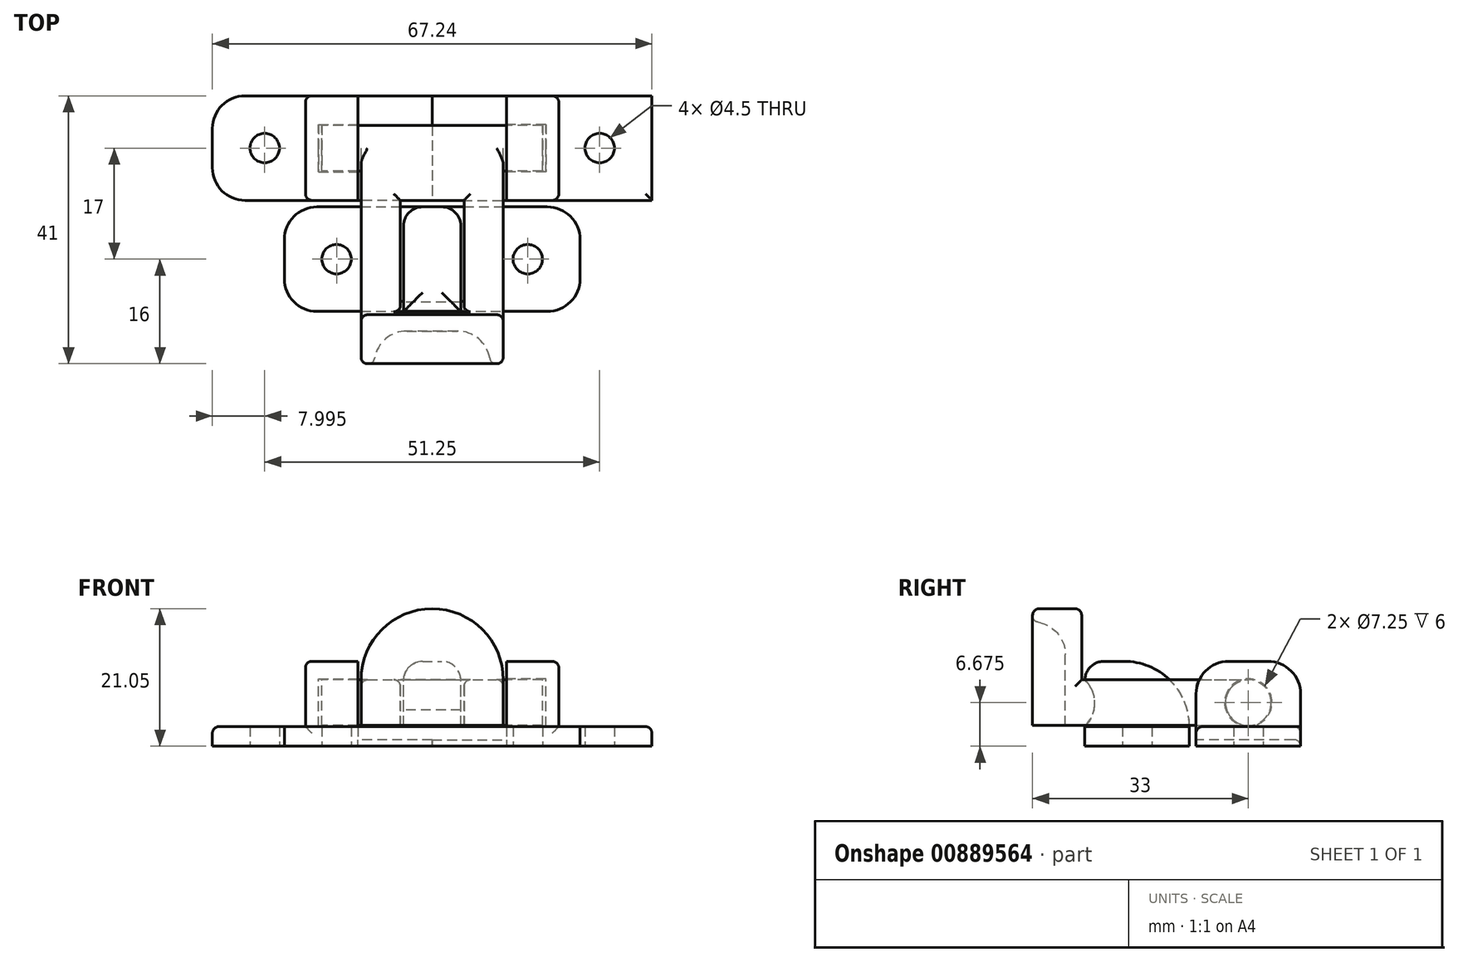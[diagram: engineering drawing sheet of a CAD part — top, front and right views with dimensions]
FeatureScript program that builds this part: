
annotation { "Feature Type Name" : "Feature", "Feature Type Description" : "" }
export const myFeature = defineFeature(function(context is Context, id is Id, definition is map)
    precondition{}
    {
        {
            var Q0;
            Q0=qCreatedBy(makeId("Top.planeOp"),FACE);
            var sketch = newSketch(context, id + "F0", { "sketchPlane" : qUnion([Q0])});
            skCircle(sketch, "E0", {"center": v(-25.62, 8.5) * mm, "radius": 2.25 * mm});
            skCircle(sketch, "E1", {"center": v(25.62, 8.5) * mm, "radius": 2.25 * mm});
            skCircle(sketch, "E2", {"center": v(-14.62, -8.5) * mm, "radius": 2.25 * mm});
            skCircle(sketch, "E3", {"center": v(14.63, -8.5) * mm, "radius": 2.25 * mm});
            skLineSegment(sketch, "E4", {"start": v(-25.62, 8.5) * mm, "end": v(25.62, 8.5) * mm, "construction": true});
            skLineSegment(sketch, "E5", {"start": v(-14.62, -8.5) * mm, "end": v(14.63, -8.5) * mm, "construction": true});
            skPoint(sketch, "E6", {"position": v(0, 8.5) * mm});
            skPoint(sketch, "E7", {"position": v(0, -8.5) * mm});
            skLineSegment(sketch, "E8.bottom", {"start": v(-33.62, 16.5) * mm, "end": v(33.62, 16.5) * mm});
            skLineSegment(sketch, "E8.top", {"start": v(-33.62, 0.5) * mm, "end": v(33.62, 0.5) * mm});
            skLineSegment(sketch, "E8.left", {"start": v(-33.63, 16.5) * mm, "end": v(-33.63, 0.5) * mm});
            skLineSegment(sketch, "E8.right", {"start": v(33.63, 16.5) * mm, "end": v(33.63, 0.5) * mm});
            skLineSegment(sketch, "E9.bottom", {"start": v(-22.62, -0.5) * mm, "end": v(22.62, -0.5) * mm});
            skLineSegment(sketch, "E9.top", {"start": v(-22.62, -16.5) * mm, "end": v(22.63, -16.5) * mm});
            skLineSegment(sketch, "E9.left", {"start": v(-22.63, -0.5) * mm, "end": v(-22.63, -16.5) * mm});
            skLineSegment(sketch, "E9.right", {"start": v(22.63, -0.5) * mm, "end": v(22.63, -16.5) * mm});
            skLineSegment(sketch, "E10", {"start": v(0, -0.5) * mm, "end": v(0, 0) * mm, "construction": true});
            skLineSegment(sketch, "E11", {"start": v(0, 0) * mm, "end": v(0, 0.5) * mm});
            skLineSegment(sketch, "E12", {"start": v(0, 0.5) * mm, "end": v(0, 0) * mm, "construction": true});
            skLineSegment(sketch, "E13", {"start": v(-11.38, 16.5) * mm, "end": v(-11.38, 0.5) * mm});
            skLineSegment(sketch, "E14", {"start": v(11.38, 16.5) * mm, "end": v(11.38, 0.5) * mm});
            skSolve(sketch);
        }
        {
            var Q0;
            Q0=makeQuery(id+"F0.imprint","IMPRINT",FACE,{"disambiguationData":[TD([[makeQuery(id+"F0.imprint","IMPRINT",EDGE,{"derivedFrom":sQuery(id+"F0.wireOp",EDGE,"E0")}),-1.0]])]});
            var Q1;
            Q1=makeQuery(id+"F0.imprint","IMPRINT",FACE,{"disambiguationData":[TD([[makeQuery(id+"F0.imprint","IMPRINT",EDGE,{"derivedFrom":sQuery(id+"F0.wireOp",EDGE,"E2")}),-1.0]])]});
            extrude(context, id + "F1", {"entities" : qUnion([Q0, Q1]), "depth" : 3 * mm, "offsetDistance" : 25 * mm});
        }
        {
            var Q0;
            Q0=makeQuery(id+"F1.opExtrude","CAP_FACE",FACE,{"disambiguationData":[OSD([sQuery(id+"F0.wireOp",EDGE,"E2"),sQuery(id+"F0.wireOp",EDGE,"E3"),sQuery(id+"F0.wireOp",EDGE,"E9.bottom"),sQuery(id+"F0.wireOp",EDGE,"E9.top"),sQuery(id+"F0.wireOp",EDGE,"E9.left"),sQuery(id+"F0.wireOp",EDGE,"E9.right")])],"isStart":false});
            var sketch = newSketch(context, id + "F2", { "sketchPlane" : qUnion([Q0])});
            skLineSegment(sketch, "E15.bottom", {"start": v(-4.38, -0.5) * mm, "end": v(4.38, -0.5) * mm});
            skLineSegment(sketch, "E15.top", {"start": v(-4.37, -16.5) * mm, "end": v(4.38, -16.5) * mm});
            skLineSegment(sketch, "E15.left", {"start": v(-4.38, -0.5) * mm, "end": v(-4.37, -16.5) * mm});
            skLineSegment(sketch, "E15.right", {"start": v(4.38, -0.5) * mm, "end": v(4.38, -16.5) * mm});
            skLineSegment(sketch, "E16", {"start": v(-4.38, -8.5) * mm, "end": v(-12.38, -8.5) * mm, "construction": true});
            skLineSegment(sketch, "E17", {"start": v(4.38, -8.5) * mm, "end": v(12.38, -8.5) * mm, "construction": true});
            skSolve(sketch);
        }
        {
            var Q0;
            Q0=makeQuery(id+"F2.imprint","IMPRINT",FACE,{"disambiguationData":[TD([[makeQuery(id+"F2.imprint","IMPRINT",EDGE,{"derivedFrom":sQuery(id+"F2.wireOp",EDGE,"E15.bottom")}),-1.0]])]});
            extrude(context, id + "F3", {"entities" : qUnion([Q0]), "operationType" : NewBodyOperationType.ADD, "depth" : 10 * mm, "offsetDistance" : 25 * mm});
        }
        {
            var Q0;
            Q0=makeQuery(id+"F3.opExtrude","SWEPT_FACE",FACE,{"disambiguationData":[OSD([sQuery(id+"F2.wireOp",EDGE,"E15.right")])]});
            var sketch = newSketch(context, id + "F4", { "sketchPlane" : qUnion([Q0])});
            skArc(sketch, "E18", {"start": v(-16.5, 3) * mm, "mid": v(-15, 6.55) * mm, "end": v(-16.5, 10.1) * mm});
            skSolve(sketch);
        }
        {
            var Q0;
            {var subQ0=sQuery(id+"F4.wireOp",EDGE,"E18");Q0=makeQuery(id+"F4.imprint","IMPRINT",FACE,{"disambiguationData":[TD([[makeQuery(id+"F4.imprint","IMPRINT",EDGE,{"derivedFrom":subQ0}),1.0]])]});}
            extrude(context, id + "F5", {"entities" : qUnion([Q0]), "operationType" : NewBodyOperationType.REMOVE, "oppositeDirection" : true, "depth" : 25 * mm, "offsetDistance" : 25 * mm});
        }
        {
            var Q0;
            Q0=makeQuery(id+"F1.opExtrude","CAP_FACE",FACE,{"disambiguationData":[OSD([sQuery(id+"F0.wireOp",EDGE,"E0"),sQuery(id+"F0.wireOp",EDGE,"E8.bottom"),sQuery(id+"F0.wireOp",EDGE,"E8.top"),sQuery(id+"F0.wireOp",EDGE,"E8.left"),sQuery(id+"F0.wireOp",EDGE,"E13")])],"isStart":false});
            var sketch = newSketch(context, id + "F6", { "sketchPlane" : qUnion([Q0])});
            skLineSegment(sketch, "E19", {"start": v(-19.37, 16.5) * mm, "end": v(-19.37, 0.5) * mm});
            skSolve(sketch);
        }
        {
            var Q0;
            {var subQ0=sQuery(id+"F6.wireOp",EDGE,"E19");Q0=makeQuery(id+"F6.imprint","IMPRINT",FACE,{"disambiguationData":[TD([[makeQuery(id+"F6.imprint","IMPRINT",EDGE,{"derivedFrom":subQ0}),1.0]])]});}
            extrude(context, id + "F7", {"entities" : qUnion([Q0]), "operationType" : NewBodyOperationType.ADD, "depth" : 10 * mm, "offsetDistance" : 25 * mm});
        }
        {
            var Q0;
            {var subQ0=sQuery(id+"F0.wireOp",EDGE,"E13");Q0=makeQuery(id+"F7.boolean.opBoolean","MERGE",FACE,{"derivedFrom":[makeQuery(id+"F1.opExtrude","SWEPT_FACE",FACE,{"disambiguationData":[OSD([subQ0])]}),makeQuery(id+"F7.opExtrude","SWEPT_FACE",FACE,{"disambiguationData":[OSD([subQ0])]})]});}
            var sketch = newSketch(context, id + "F8", { "sketchPlane" : qUnion([Q0])});
            skCircle(sketch, "E20", {"center": v(8.5, 6.68) * mm, "radius": 3.62 * mm});
            skPoint(sketch, "E21", {"position": v(8.5, 13) * mm});
            skSolve(sketch);
        }
        {
            var Q0;
            Q0=makeQuery(id+"F8.imprint","IMPRINT",FACE,{"disambiguationData":[TD([[makeQuery(id+"F8.imprint","IMPRINT",EDGE,{"derivedFrom":sQuery(id+"F8.wireOp",EDGE,"E20")}),1.0]])]});
            extrude(context, id + "F9", {"entities" : qUnion([Q0]), "operationType" : NewBodyOperationType.REMOVE, "oppositeDirection" : true, "depth" : 6 * mm, "offsetDistance" : 25 * mm});
        }
        {
            var Q0;
            Q0=makeQuery(id+"F9.boolean.opBoolean","COPY",FACE,{"derivedFrom":makeQuery(id+"F9.opExtrude","CAP_FACE",FACE,{"disambiguationData":[OSD([sQuery(id+"F8.wireOp",EDGE,"E20")])],"isStart":false})});
            cPlane(context, id + "F10", {"entities" : qUnion([Q0]), "cplaneType" : CPlaneType.OFFSET, "offset" : .5 * mm, "width" : 150 * mm, "height" : 150 * mm});
        }
        {
            var Q0;
            {var subQ0=sQuery(id+"F0.wireOp",EDGE,"E13");Q0=makeQuery(id+"F7.boolean.opBoolean","MERGE",FACE,{"derivedFrom":[makeQuery(id+"F1.opExtrude","SWEPT_FACE",FACE,{"disambiguationData":[OSD([subQ0])]}),makeQuery(id+"F7.opExtrude","SWEPT_FACE",FACE,{"disambiguationData":[OSD([subQ0])]})]});}
            var sketch = newSketch(context, id + "F11", { "sketchPlane" : qUnion([Q0])});
            skLineSegment(sketch, "E22", {"start": v(16.5, 1) * mm, "end": v(0.5, 1) * mm});
            skSolve(sketch);
        }
        {
            var Q0;
            {var subQ0=sQuery(id+"F11.wireOp",EDGE,"E22");Q0=makeQuery(id+"F11.imprint","IMPRINT",FACE,{"disambiguationData":[TD([[makeQuery(id+"F11.imprint","IMPRINT",EDGE,{"derivedFrom":subQ0}),1.0]])]});}
            var Q1;
            Q1=qCreatedBy(makeId("Right.planeOp"),FACE);
            extrude(context, id + "F12", {"entities" : qUnion([Q0]), "operationType" : NewBodyOperationType.ADD, "endBound" : BoundingType.UP_TO_SURFACE, "depth" : 25 * mm, "endBoundEntityFace" : qUnion([Q1]), "offsetDistance" : 25 * mm});
        }
        {
            var Q0;
            Q0=makeQuery(id+"F1.opExtrude","SWEPT_BODY",BODY,{"disambiguationData":[OSD([sQuery(id+"F0.wireOp",EDGE,"E0"),sQuery(id+"F0.wireOp",EDGE,"E8.bottom"),sQuery(id+"F0.wireOp",EDGE,"E8.top"),sQuery(id+"F0.wireOp",EDGE,"E8.left"),sQuery(id+"F0.wireOp",EDGE,"E13")])]});
            var Q1;
            Q1=qCreatedBy(makeId("Right.planeOp"),FACE);
            mirror(context, id + "F13", {"operationType" : NewBodyOperationType.ADD, "entities" : qUnion([Q0]), "mirrorPlane" : qUnion([Q1])});
        }
        {
            var Q0;
            Q0=qCreatedBy(id+"F10.planeOp",FACE);
            var sketch = newSketch(context, id + "F14", { "sketchPlane" : qUnion([Q0])});
            skCircle(sketch, "E23", {"center": v(8.5, 6.68) * mm, "radius": 3.5 * mm});
            skSolve(sketch);
        }
        {
            var Q0;
            Q0=makeQuery(id+"F14.imprint","IMPRINT",FACE,{"disambiguationData":[TD([[makeQuery(id+"F14.imprint","IMPRINT",EDGE,{"derivedFrom":sQuery(id+"F14.wireOp",EDGE,"E23")}),1.0]])]});
            var Q1;
            Q1=qCreatedBy(makeId("Right.planeOp"),FACE);
            extrude(context, id + "F15", {"entities" : qUnion([Q0]), "endBound" : BoundingType.UP_TO_SURFACE, "depth" : 30 * mm, "endBoundEntityFace" : qUnion([Q1]), "offsetDistance" : 25 * mm});
        }
        {
            var Q0;
            Q0=makeQuery(id+"F15.opExtrude","CAP_FACE",FACE,{"disambiguationData":[OSD([sQuery(id+"F14.wireOp",EDGE,"E23")])],"isStart":false});
            var sketch = newSketch(context, id + "F16", { "sketchPlane" : qUnion([Q0])});
            skLineSegment(sketch, "E24", {"start": v(8.5, 10.18) * mm, "end": v(0.5, 10.18) * mm});
            skLineSegment(sketch, "E25", {"start": v(8.5, 3.18) * mm, "end": v(0.5, 3.17) * mm});
            skLineSegment(sketch, "E26", {"start": v(0.5, 10.18) * mm, "end": v(0.5, 3.17) * mm});
            skArc(sketch, "E27", {"start": v(8.5, 3.18) * mm, "mid": v(12, 6.68) * mm, "end": v(8.5, 10.18) * mm});
            skSolve(sketch);
        }
        {
            var Q0;
            {var subQ0=sQuery(id+"F16.wireOp",EDGE,"E24");Q0=makeQuery(id+"F16.imprint","IMPRINT",FACE,{"disambiguationData":[TD([[makeQuery(id+"F16.imprint","IMPRINT",EDGE,{"derivedFrom":subQ0}),1.0]])]});}
            var Q1;
            {var subQ0=sQuery(id+"F0.wireOp",EDGE,"E13");Q1=makeQuery(id+"F7.boolean.opBoolean","MERGE",FACE,{"derivedFrom":[makeQuery(id+"F1.opExtrude","SWEPT_FACE",FACE,{"disambiguationData":[OSD([subQ0])]}),makeQuery(id+"F7.opExtrude","SWEPT_FACE",FACE,{"disambiguationData":[OSD([subQ0])]})]});}
            extrude(context, id + "F17", {"entities" : qUnion([Q0]), "operationType" : NewBodyOperationType.ADD, "endBound" : BoundingType.UP_TO_SURFACE, "oppositeDirection" : true, "depth" : 25 * mm, "endBoundEntityFace" : qUnion([Q1]), "hasOffset" : true, "offsetDistance" : .5 * mm});
        }
        {
            var Q0;
            Q0=makeQuery(id+"F17.opExtrude","SWEPT_FACE",FACE,{"disambiguationData":[OSD([sQuery(id+"F16.wireOp",EDGE,"E26")])]});
            var sketch = newSketch(context, id + "F18", { "sketchPlane" : qUnion([Q0])});
            skLineSegment(sketch, "E28", {"start": v(-4.87, 10.18) * mm, "end": v(-4.87, 3.17) * mm});
            skSolve(sketch);
        }
        {
            var Q0;
            {var subQ0=sQuery(id+"F18.wireOp",EDGE,"E28");Q0=makeQuery(id+"F18.imprint","IMPRINT",FACE,{"disambiguationData":[TD([[makeQuery(id+"F18.imprint","IMPRINT",EDGE,{"derivedFrom":subQ0}),-1.0]])]});}
            extrude(context, id + "F19", {"entities" : qUnion([Q0]), "operationType" : NewBodyOperationType.ADD, "depth" : 25 * mm, "offsetDistance" : 25 * mm});
        }
        {
            var Q0;
            Q0=makeQuery(id+"F19.opExtrude","SWEPT_FACE",FACE,{"disambiguationData":[OSD([sQuery(id+"F18.wireOp",EDGE,"E28")])]});
            var sketch = newSketch(context, id + "F20", { "sketchPlane" : qUnion([Q0])});
            skArc(sketch, "E29", {"start": v(-16.44, 3.17) * mm, "mid": v(-14.98, 6.7) * mm, "end": v(-16.55, 10.18) * mm});
            skSolve(sketch);
        }
        {
            var Q0;
            {var subQ0=sQuery(id+"F20.wireOp",EDGE,"E29");Q0=makeQuery(id+"F20.imprint","IMPRINT",FACE,{"disambiguationData":[TD([[makeQuery(id+"F20.imprint","IMPRINT",EDGE,{"derivedFrom":subQ0}),1.0]])]});}
            var Q1;
            {var subQ0=sQuery(id+"F14.wireOp",EDGE,"E23");Q1=makeQuery(id+"F17.boolean.opBoolean","MERGE",FACE,{"derivedFrom":[makeQuery(id+"F15.opExtrude","CAP_FACE",FACE,{"disambiguationData":[OSD([subQ0])],"isStart":false}),makeQuery(id+"F17.opExtrude","CAP_FACE",FACE,{"disambiguationData":[OSD([subQ0,sQuery(id+"F16.wireOp",EDGE,"E24"),sQuery(id+"F16.wireOp",EDGE,"E25"),sQuery(id+"F16.wireOp",EDGE,"E26")])],"isStart":true})]});}
            extrude(context, id + "F21", {"entities" : qUnion([Q0]), "endBound" : BoundingType.UP_TO_SURFACE, "depth" : 25 * mm, "endBoundEntityFace" : qUnion([Q1]), "offsetDistance" : 25 * mm});
        }
        {
            var Q0;
            Q0=makeQuery(id+"F15.opExtrude","SWEPT_BODY",BODY,{"disambiguationData":[OSD([sQuery(id+"F14.wireOp",EDGE,"E23")])]});
            var Q1;
            Q1=makeQuery(id+"F21.opExtrude","SWEPT_BODY",BODY,{"disambiguationData":[OSD([sQuery(id+"F16.wireOp",EDGE,"E24"),sQuery(id+"F16.wireOp",EDGE,"E25"),sQuery(id+"F16.wireOp",EDGE,"E26"),sQuery(id+"F18.wireOp",EDGE,"E28"),sQuery(id+"F20.wireOp",EDGE,"E29")])]});
            var Q2;
            Q2=qCreatedBy(makeId("Right.planeOp"),FACE);
            mirror(context, id + "F22", {"operationType" : NewBodyOperationType.ADD, "entities" : qUnion([Q0, Q1]), "mirrorPlane" : qUnion([Q2])});
        }
        {
            var Q0;
            {var subQ0=sQuery(id+"F18.wireOp",EDGE,"E28");var subQ1=makeQuery(id+"F21.opExtrude","SWEPT_FACE",FACE,{"disambiguationData":[OSD([subQ0])]});var subQ2=makeQuery(id+"F19.opExtrude","CAP_FACE",FACE,{"disambiguationData":[OSD([sQuery(id+"F16.wireOp",EDGE,"E24"),sQuery(id+"F16.wireOp",EDGE,"E25"),sQuery(id+"F16.wireOp",EDGE,"E26"),subQ0])],"isStart":false});Q0=makeQuery(id+"F22.boolean.opBoolean","MERGE",FACE,{"derivedFrom":[subQ2,subQ1,makeQuery(id+"F22.opPattern","COPY",FACE,{"derivedFrom":subQ2,"instanceName":"1"}),makeQuery(id+"F22.opPattern","COPY",FACE,{"derivedFrom":subQ1,"instanceName":"1"})]});}
            var sketch = newSketch(context, id + "F23", { "sketchPlane" : qUnion([Q0])});
            skArc(sketch, "E30", {"start": v(10.87, 10.18) * mm, "mid": v(0, 21.05) * mm, "end": v(-10.87, 10.18) * mm});
            skSolve(sketch);
        }
        {
            var Q0;
            Q0=qSketchRegion(id+"F23",true);
            var Q1;
            Q1=makeQuery(id+"F23.imprint","IMPRINT",FACE,{"disambiguationData":[TD([[makeQuery(id+"F23.imprint","IMPRINT",EDGE,{"derivedFrom":sQuery(id+"F23.wireOp",EDGE,"E30")}),1.0]])]});
            extrude(context, id + "F24", {"entities" : qUnion([Q0, Q1]), "operationType" : NewBodyOperationType.ADD, "depth" : -7.5 * mm, "offsetDistance" : 25 * mm});
        }
        {
            var Q0;
            {var subQ0=sQuery(id+"F18.wireOp",EDGE,"E28");var subQ1=sQuery(id+"F16.wireOp",EDGE,"E26");var subQ2=sQuery(id+"F16.wireOp",EDGE,"E24");var subQ3=makeQuery(id+"F21.opExtrude","SWEPT_FACE",FACE,{"disambiguationData":[OSD([subQ0])]});var subQ4=makeQuery(id+"F19.opExtrude","CAP_FACE",FACE,{"disambiguationData":[OSD([subQ2,sQuery(id+"F16.wireOp",EDGE,"E25"),subQ1,subQ0])],"isStart":false});Q0=makeQuery(id+"F24.boolean.opBoolean","MERGE",FACE,{"derivedFrom":[makeQuery(id+"F22.boolean.opBoolean","MERGE",FACE,{"derivedFrom":[subQ4,subQ3,makeQuery(id+"F22.opPattern","COPY",FACE,{"derivedFrom":subQ4,"instanceName":"1"}),makeQuery(id+"F22.opPattern","COPY",FACE,{"derivedFrom":subQ3,"instanceName":"1"})]}),makeQuery(id+"F24.opExtrude","CAP_FACE",FACE,{"disambiguationData":[OSD([subQ2,subQ1,subQ0,sQuery(id+"F23.wireOp",EDGE,"E30")])],"isStart":true})]});}
            var sketch = newSketch(context, id + "F25", { "sketchPlane" : qUnion([Q0])});
            skLineSegment(sketch, "E31.0", {"start": v(8.87, 3.17) * mm, "end": v(8.87, 10.18) * mm});
            skArc(sketch, "E31.1", {"start": v(8.87, 10.18) * mm, "mid": v(0, 19.05) * mm, "end": v(-8.87, 10.18) * mm});
            skLineSegment(sketch, "E31.2", {"start": v(-8.87, 3.17) * mm, "end": v(-8.87, 10.18) * mm});
            skSolve(sketch);
        }
        {
            var Q0;
            {var subQ0=sQuery(id+"F25.wireOp",EDGE,"E31.0");Q0=makeQuery(id+"F25.imprint","IMPRINT",FACE,{"disambiguationData":[TD([[makeQuery(id+"F25.imprint","IMPRINT",EDGE,{"derivedFrom":subQ0}),1.0]])]});}
            extrude(context, id + "F26", {"entities" : qUnion([Q0]), "operationType" : NewBodyOperationType.REMOVE, "oppositeDirection" : true, "depth" : 5 * mm, "offsetDistance" : 25 * mm});
        }
        {
            var Q0;
            Q0=makeQuery(id+"F7.opExtrude","CAP_EDGE",EDGE,{"disambiguationData":[OSD([sQuery(id+"F0.wireOp",EDGE,"E8.bottom")])],"isStart":false});
            var Q1;
            Q1=makeQuery(id+"F7.opExtrude","CAP_EDGE",EDGE,{"disambiguationData":[OSD([sQuery(id+"F0.wireOp",EDGE,"E8.top")])],"isStart":false});
            var Q2;
            Q2=makeQuery(id+"F13.opPattern","COPY",EDGE,{"derivedFrom":makeQuery(id+"F7.opExtrude","CAP_EDGE",EDGE,{"disambiguationData":[OSD([sQuery(id+"F0.wireOp",EDGE,"E8.bottom")])],"isStart":false}),"instanceName":"1"});
            var Q3;
            Q3=makeQuery(id+"F13.opPattern","COPY",EDGE,{"derivedFrom":makeQuery(id+"F7.opExtrude","CAP_EDGE",EDGE,{"disambiguationData":[OSD([sQuery(id+"F0.wireOp",EDGE,"E8.top")])],"isStart":false}),"instanceName":"1"});
            fillet(context, id + "F27", {"entities" : qUnion([Q0, Q1, Q2, Q3]), "radius" : 5 * mm, "tangentPropagation" : true, "allowEdgeOverflow" : false});
        }
        {
            var Q0;
            Q0=makeQuery(id+"F3.opExtrude","CAP_EDGE",EDGE,{"disambiguationData":[OSD([sQuery(id+"F2.wireOp",EDGE,"E15.top")])],"isStart":false});
            fillet(context, id + "F28", {"entities" : qUnion([Q0]), "radius" : 2.9 * mm, "tangentPropagation" : true, "allowEdgeOverflow" : false});
        }
        {
            var Q0;
            Q0=makeQuery(id+"F1.opExtrude","CAP_EDGE",EDGE,{"disambiguationData":[OSD([sQuery(id+"F0.wireOp",EDGE,"E8.top")])],"isStart":false});
            var Q1;
            Q1=makeQuery(id+"F1.opExtrude","CAP_EDGE",EDGE,{"disambiguationData":[OSD([sQuery(id+"F0.wireOp",EDGE,"E8.left")])],"isStart":false});
            var Q2;
            Q2=makeQuery(id+"F1.opExtrude","CAP_EDGE",EDGE,{"disambiguationData":[OSD([sQuery(id+"F0.wireOp",EDGE,"E8.bottom")])],"isStart":false});
            var Q3;
            Q3=makeQuery(id+"F27.opFillet","BLEND_EDGE",EDGE,{"blendedFrom":[makeQuery(id+"F7.opExtrude","CAP_EDGE",EDGE,{"disambiguationData":[OSD([sQuery(id+"F0.wireOp",EDGE,"E8.top")])],"isStart":false}),makeQuery(id+"F7.opExtrude","SWEPT_FACE",FACE,{"disambiguationData":[OSD([sQuery(id+"F6.wireOp",EDGE,"E19")])]})],"blendedInto":[makeQuery(id+"F7.opExtrude","SWEPT_FACE",FACE,{"disambiguationData":[OSD([sQuery(id+"F6.wireOp",EDGE,"E19")])]})]});
            var Q4;
            Q4=makeQuery(id+"F7.opExtrude","CAP_EDGE",EDGE,{"disambiguationData":[OSD([sQuery(id+"F6.wireOp",EDGE,"E19")])],"isStart":true});
            var Q5;
            Q5=makeQuery(id+"F13.opPattern","COPY",EDGE,{"derivedFrom":makeQuery(id+"F7.opExtrude","SWEPT_EDGE",EDGE,{"disambiguationData":[OSD([sQuery(id+"F0.wireOp",EDGE,"E8.top"),sQuery(id+"F6.wireOp",EDGE,"E19")])]}),"instanceName":"1"});
            var Q6;
            Q6=makeQuery(id+"F13.opPattern","COPY",EDGE,{"derivedFrom":makeQuery(id+"F7.opExtrude","CAP_EDGE",EDGE,{"disambiguationData":[OSD([sQuery(id+"F6.wireOp",EDGE,"E19")])],"isStart":true}),"instanceName":"1"});
            var Q7;
            Q7=makeQuery(id+"F13.opPattern","COPY",EDGE,{"derivedFrom":makeQuery(id+"F1.opExtrude","CAP_EDGE",EDGE,{"disambiguationData":[OSD([sQuery(id+"F0.wireOp",EDGE,"E8.top")])],"isStart":false}),"instanceName":"1"});
            var Q8;
            Q8=makeQuery(id+"F13.opPattern","COPY",EDGE,{"derivedFrom":makeQuery(id+"F1.opExtrude","CAP_EDGE",EDGE,{"disambiguationData":[OSD([sQuery(id+"F0.wireOp",EDGE,"E8.left")])],"isStart":false}),"instanceName":"1"});
            var Q9;
            {var subQ0=sQuery(id+"F0.wireOp",EDGE,"E9.left");var subQ1=sQuery(id+"F0.wireOp",EDGE,"E9.bottom");Q9=makeQuery(id+"F3.boolean.opBoolean","SPLIT",EDGE,{"disambiguationData":[TD([makeQuery(id+"F1.opExtrude","SWEPT_FACE",FACE,{"disambiguationData":[OSD([subQ0])]})])],"derivedFrom":makeQuery(id+"F1.opExtrude","CAP_EDGE",EDGE,{"disambiguationData":[OSD([subQ1])],"isStart":false})});}
            var Q10;
            {var subQ0=sQuery(id+"F0.wireOp",EDGE,"E9.left");var subQ1=sQuery(id+"F0.wireOp",EDGE,"E9.top");Q10=makeQuery(id+"F3.boolean.opBoolean","SPLIT",EDGE,{"disambiguationData":[TD([makeQuery(id+"F1.opExtrude","SWEPT_FACE",FACE,{"disambiguationData":[OSD([subQ0])]})])],"derivedFrom":makeQuery(id+"F1.opExtrude","CAP_EDGE",EDGE,{"disambiguationData":[OSD([subQ1])],"isStart":false})});}
            var Q11;
            Q11=makeQuery(id+"F1.opExtrude","CAP_EDGE",EDGE,{"disambiguationData":[OSD([sQuery(id+"F0.wireOp",EDGE,"E9.left")])],"isStart":false});
            var Q12;
            {var subQ0=sQuery(id+"F0.wireOp",EDGE,"E9.right");var subQ1=sQuery(id+"F0.wireOp",EDGE,"E9.top");Q12=makeQuery(id+"F3.boolean.opBoolean","SPLIT",EDGE,{"disambiguationData":[TD([makeQuery(id+"F1.opExtrude","SWEPT_FACE",FACE,{"disambiguationData":[OSD([subQ0])]})])],"derivedFrom":makeQuery(id+"F1.opExtrude","CAP_EDGE",EDGE,{"disambiguationData":[OSD([subQ1])],"isStart":false})});}
            var Q13;
            {var subQ0=sQuery(id+"F0.wireOp",EDGE,"E9.right");var subQ1=sQuery(id+"F0.wireOp",EDGE,"E9.bottom");Q13=makeQuery(id+"F3.boolean.opBoolean","SPLIT",EDGE,{"disambiguationData":[TD([makeQuery(id+"F1.opExtrude","SWEPT_FACE",FACE,{"disambiguationData":[OSD([subQ0])]})])],"derivedFrom":makeQuery(id+"F1.opExtrude","CAP_EDGE",EDGE,{"disambiguationData":[OSD([subQ1])],"isStart":false})});}
            var Q14;
            Q14=makeQuery(id+"F1.opExtrude","CAP_EDGE",EDGE,{"disambiguationData":[OSD([sQuery(id+"F0.wireOp",EDGE,"E9.right")])],"isStart":false});
            var Q15;
            Q15=makeQuery(id+"F12.opExtrude","CAP_EDGE",EDGE,{"disambiguationData":[OSD([sQuery(id+"F11.wireOp",EDGE,"E22")])],"isStart":true});
            var Q16;
            Q16=makeQuery(id+"F13.opPattern","COPY",EDGE,{"derivedFrom":makeQuery(id+"F12.opExtrude","CAP_EDGE",EDGE,{"disambiguationData":[OSD([sQuery(id+"F11.wireOp",EDGE,"E22")])],"isStart":true}),"instanceName":"1"});
            var Q17;
            {var subQ0=makeQuery(id+"F12.opExtrude","SWEPT_EDGE",EDGE,{"disambiguationData":[OSD([sQuery(id+"F0.wireOp",EDGE,"E8.bottom"),sQuery(id+"F0.wireOp",EDGE,"E13"),sQuery(id+"F11.wireOp",EDGE,"E22")])]});Q17=makeQuery(id+"F13.boolean.opBoolean","MERGE",EDGE,{"derivedFrom":[subQ0,makeQuery(id+"F13.opPattern","COPY",EDGE,{"derivedFrom":subQ0,"instanceName":"1"})]});}
            fillet(context, id + "F29", {"entities" : qUnion([Q0, Q1, Q2, Q3, Q4, Q5, Q6, Q7, Q8, Q9, Q10, Q11, Q12, Q13, Q14, Q15, Q16, Q17]), "radius" : 1 * mm, "tangentPropagation" : true, "allowEdgeOverflow" : false});
        }
        {
            var Q0;
            Q0=makeQuery(id+"F3.opExtrude","CAP_EDGE",EDGE,{"disambiguationData":[OSD([sQuery(id+"F2.wireOp",EDGE,"E15.bottom")])],"isStart":false});
            fillet(context, id + "F30", {"entities" : qUnion([Q0]), "radius" : 10 * mm, "tangentPropagation" : true, "allowEdgeOverflow" : false});
        }
        {
            var Q0;
            Q0=makeQuery(id+"F3.opExtrude","CAP_EDGE",EDGE,{"disambiguationData":[OSD([sQuery(id+"F2.wireOp",EDGE,"E15.left")])],"isStart":false});
            var Q1;
            Q1=makeQuery(id+"F3.opExtrude","CAP_EDGE",EDGE,{"disambiguationData":[OSD([sQuery(id+"F2.wireOp",EDGE,"E15.right")])],"isStart":false});
            fillet(context, id + "F31", {"entities" : qUnion([Q0, Q1]), "radius" : 2.9 * mm, "tangentPropagation" : true, "allowEdgeOverflow" : false});
        }
        {
            var Q0;
            Q0=makeQuery(id+"F26.boolean.opBoolean","COPY",EDGE,{"derivedFrom":makeQuery(id+"F26.opExtrude","CAP_EDGE",EDGE,{"disambiguationData":[OSD([sQuery(id+"F25.wireOp",EDGE,"E31.2")])],"isStart":false})});
            var Q1;
            Q1=makeQuery(id+"F26.boolean.opBoolean","COPY",EDGE,{"derivedFrom":makeQuery(id+"F26.opExtrude","CAP_EDGE",EDGE,{"disambiguationData":[OSD([sQuery(id+"F25.wireOp",EDGE,"E31.1")])],"isStart":false})});
            fillet(context, id + "F32", {"entities" : qUnion([Q0, Q1]), "radius" : 5 * mm, "tangentPropagation" : true, "allowEdgeOverflow" : false});
        }
        {
            var Q0;
            Q0=makeQuery(id+"F19.opExtrude","CAP_EDGE",EDGE,{"disambiguationData":[OSD([sQuery(id+"F16.wireOp",EDGE,"E26")])],"isStart":false});
            var Q1;
            Q1=makeQuery(id+"F24.opExtrude","CAP_EDGE",EDGE,{"disambiguationData":[OSD([sQuery(id+"F23.wireOp",EDGE,"E30")])],"isStart":true});
            var Q2;
            {var subQ0=sQuery(id+"F18.wireOp",EDGE,"E28");var subQ1=sQuery(id+"F16.wireOp",EDGE,"E26");var subQ2=sQuery(id+"F16.wireOp",EDGE,"E24");var subQ3=makeQuery(id+"F21.opExtrude","SWEPT_FACE",FACE,{"disambiguationData":[OSD([subQ0])]});var subQ4=makeQuery(id+"F19.opExtrude","CAP_FACE",FACE,{"disambiguationData":[OSD([subQ2,sQuery(id+"F16.wireOp",EDGE,"E25"),subQ1,subQ0])],"isStart":false});Q2=makeQuery(id+"F32.opFillet","BLEND_EDGE",EDGE,{"blendedFrom":[makeQuery(id+"F26.boolean.opBoolean","COPY",EDGE,{"derivedFrom":makeQuery(id+"F26.opExtrude","CAP_EDGE",EDGE,{"disambiguationData":[OSD([sQuery(id+"F25.wireOp",EDGE,"E31.0")])],"isStart":false})}),makeQuery(id+"F24.boolean.opBoolean","MERGE",FACE,{"derivedFrom":[makeQuery(id+"F22.boolean.opBoolean","MERGE",FACE,{"derivedFrom":[subQ4,subQ3,makeQuery(id+"F22.opPattern","COPY",FACE,{"derivedFrom":subQ4,"instanceName":"1"}),makeQuery(id+"F22.opPattern","COPY",FACE,{"derivedFrom":subQ3,"instanceName":"1"})]}),makeQuery(id+"F24.opExtrude","CAP_FACE",FACE,{"disambiguationData":[OSD([subQ2,subQ1,subQ0,sQuery(id+"F23.wireOp",EDGE,"E30")])],"isStart":true})]})],"blendedInto":[makeQuery(id+"F24.boolean.opBoolean","MERGE",FACE,{"derivedFrom":[makeQuery(id+"F22.boolean.opBoolean","MERGE",FACE,{"derivedFrom":[subQ4,subQ3,makeQuery(id+"F22.opPattern","COPY",FACE,{"derivedFrom":subQ4,"instanceName":"1"}),makeQuery(id+"F22.opPattern","COPY",FACE,{"derivedFrom":subQ3,"instanceName":"1"})]}),makeQuery(id+"F24.opExtrude","CAP_FACE",FACE,{"disambiguationData":[OSD([subQ2,subQ1,subQ0,sQuery(id+"F23.wireOp",EDGE,"E30")])],"isStart":true})]})]});}
            var Q3;
            Q3=makeQuery(id+"F24.opExtrude","CAP_EDGE",EDGE,{"disambiguationData":[OSD([sQuery(id+"F23.wireOp",EDGE,"E30")])],"isStart":false});
            var Q4;
            {var subQ0=sQuery(id+"F16.wireOp",EDGE,"E24");Q4=makeQuery(id+"F24.boolean.opBoolean","SPLIT",EDGE,{"derivedFrom":makeQuery(id+"F19.boolean.opBoolean","MERGE",EDGE,{"derivedFrom":[makeQuery(id+"F17.opExtrude","CAP_EDGE",EDGE,{"disambiguationData":[OSD([subQ0])],"isStart":false}),makeQuery(id+"F19.opExtrude","SWEPT_EDGE",EDGE,{"disambiguationData":[OSD([subQ0,sQuery(id+"F16.wireOp",EDGE,"E26")])]})]})});}
            var Q5;
            Q5=makeQuery(id+"F19.opExtrude","SWEPT_EDGE",EDGE,{"disambiguationData":[OSD([sQuery(id+"F16.wireOp",EDGE,"E24"),sQuery(id+"F16.wireOp",EDGE,"E26"),sQuery(id+"F18.wireOp",EDGE,"E28")])]});
            var Q6;
            {var subQ0=makeQuery(id+"F17.opExtrude","SWEPT_EDGE",EDGE,{"disambiguationData":[OSD([sQuery(id+"F16.wireOp",EDGE,"E24"),sQuery(id+"F16.wireOp",EDGE,"E26")])]});Q6=makeQuery(id+"F22.boolean.opBoolean","MERGE",EDGE,{"derivedFrom":[subQ0,makeQuery(id+"F22.opPattern","COPY",EDGE,{"derivedFrom":subQ0,"instanceName":"1"})]});}
            var Q7;
            Q7=makeQuery(id+"F22.opPattern","COPY",EDGE,{"derivedFrom":makeQuery(id+"F19.opExtrude","SWEPT_EDGE",EDGE,{"disambiguationData":[OSD([sQuery(id+"F16.wireOp",EDGE,"E24"),sQuery(id+"F16.wireOp",EDGE,"E26"),sQuery(id+"F18.wireOp",EDGE,"E28")])]}),"instanceName":"1"});
            var Q8;
            {var subQ0=sQuery(id+"F16.wireOp",EDGE,"E24");Q8=makeQuery(id+"F24.boolean.opBoolean","SPLIT",EDGE,{"derivedFrom":makeQuery(id+"F22.opPattern","COPY",EDGE,{"derivedFrom":makeQuery(id+"F19.boolean.opBoolean","MERGE",EDGE,{"derivedFrom":[makeQuery(id+"F17.opExtrude","CAP_EDGE",EDGE,{"disambiguationData":[OSD([subQ0])],"isStart":false}),makeQuery(id+"F19.opExtrude","SWEPT_EDGE",EDGE,{"disambiguationData":[OSD([subQ0,sQuery(id+"F16.wireOp",EDGE,"E26")])]})]}),"instanceName":"1"})});}
            var Q9;
            Q9=makeQuery(id+"F22.opPattern","COPY",EDGE,{"derivedFrom":makeQuery(id+"F19.opExtrude","CAP_EDGE",EDGE,{"disambiguationData":[OSD([sQuery(id+"F18.wireOp",EDGE,"E28")])],"isStart":true}),"instanceName":"1"});
            var Q10;
            Q10=makeQuery(id+"F19.opExtrude","CAP_EDGE",EDGE,{"disambiguationData":[OSD([sQuery(id+"F18.wireOp",EDGE,"E28")])],"isStart":true});
            fillet(context, id + "F33", {"entities" : qUnion([Q0, Q1, Q2, Q3, Q4, Q5, Q6, Q7, Q8, Q9, Q10]), "radius" : 1 * mm, "tangentPropagation" : true, "allowEdgeOverflow" : false});
        }
        {
            var Q0;
            Q0=makeQuery(id+"F1.opExtrude","SWEPT_EDGE",EDGE,{"disambiguationData":[OSD([sQuery(id+"F0.wireOp",EDGE,"E8.bottom"),sQuery(id+"F0.wireOp",EDGE,"E8.left")])]});
            var Q1;
            Q1=makeQuery(id+"F1.opExtrude","SWEPT_EDGE",EDGE,{"disambiguationData":[OSD([sQuery(id+"F0.wireOp",EDGE,"E8.top"),sQuery(id+"F0.wireOp",EDGE,"E8.left")])]});
            var Q2;
            Q2=makeQuery(id+"F1.opExtrude","SWEPT_EDGE",EDGE,{"disambiguationData":[OSD([sQuery(id+"F0.wireOp",EDGE,"E9.bottom"),sQuery(id+"F0.wireOp",EDGE,"E9.left")])]});
            var Q3;
            Q3=makeQuery(id+"F1.opExtrude","SWEPT_EDGE",EDGE,{"disambiguationData":[OSD([sQuery(id+"F0.wireOp",EDGE,"E9.top"),sQuery(id+"F0.wireOp",EDGE,"E9.left")])]});
            var Q4;
            Q4=makeQuery(id+"F1.opExtrude","SWEPT_EDGE",EDGE,{"disambiguationData":[OSD([sQuery(id+"F0.wireOp",EDGE,"E9.top"),sQuery(id+"F0.wireOp",EDGE,"E9.right")])]});
            var Q5;
            Q5=makeQuery(id+"F1.opExtrude","SWEPT_EDGE",EDGE,{"disambiguationData":[OSD([sQuery(id+"F0.wireOp",EDGE,"E9.bottom"),sQuery(id+"F0.wireOp",EDGE,"E9.right")])]});
            var Q6;
            Q6=makeQuery(id+"F13.opPattern","COPY",EDGE,{"derivedFrom":makeQuery(id+"F1.opExtrude","SWEPT_EDGE",EDGE,{"disambiguationData":[OSD([sQuery(id+"F0.wireOp",EDGE,"E8.bottom"),sQuery(id+"F0.wireOp",EDGE,"E8.left")])]}),"instanceName":"1"});
            var Q7;
            Q7=makeQuery(id+"F13.opPattern","COPY",EDGE,{"derivedFrom":makeQuery(id+"F1.opExtrude","SWEPT_EDGE",EDGE,{"disambiguationData":[OSD([sQuery(id+"F0.wireOp",EDGE,"E8.top"),sQuery(id+"F0.wireOp",EDGE,"E8.left")])]}),"instanceName":"1"});
            fillet(context, id + "F34", {"entities" : qUnion([Q0, Q1, Q2, Q3, Q4, Q5, Q6, Q7]), "radius" : 5 * mm, "tangentPropagation" : true, "allowEdgeOverflow" : false});
        }
    });
